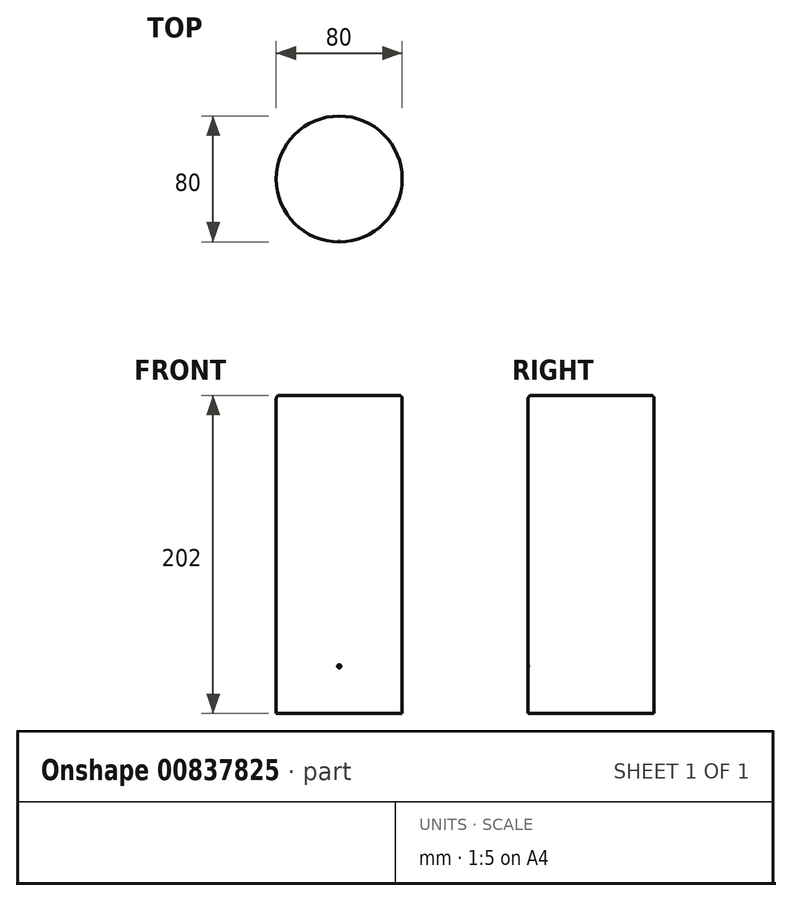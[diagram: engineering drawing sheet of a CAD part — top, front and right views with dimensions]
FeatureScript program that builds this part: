
annotation { "Feature Type Name" : "Feature", "Feature Type Description" : "" }
export const myFeature = defineFeature(function(context is Context, id is Id, definition is map)
    precondition{}
    {
        {
            var Q0;
            Q0=qCreatedBy(makeId("Front.planeOp"),FACE);
            var sketch = newSketch(context, id + "F0", { "sketchPlane" : qUnion([Q0])});
            skLineSegment(sketch, "E0", {"start": v(0, 0) * mm, "end": v(40, 0) * mm});
            skLineSegment(sketch, "E1", {"start": v(40, 0) * mm, "end": v(40, 50) * mm});
            skLineSegment(sketch, "E2", {"start": v(40, 50) * mm, "end": v(40, -150) * mm});
            skLineSegment(sketch, "E3", {"start": v(0, 0) * mm, "end": v(-40, 0) * mm});
            skLineSegment(sketch, "E4", {"start": v(-40, 0) * mm, "end": v(-40, 50) * mm});
            skLineSegment(sketch, "E5", {"start": v(-40, 50) * mm, "end": v(-40, -150) * mm});
            skLineSegment(sketch, "E6", {"start": v(-40, 50) * mm, "end": v(40, 50) * mm});
            skLineSegment(sketch, "E7", {"start": v(-40, -150) * mm, "end": v(40, -150) * mm});
            skLineSegment(sketch, "E8", {"start": v(0, 69.2) * mm, "end": v(0, -177.13) * mm});
            skPoint(sketch, "E8.startSnap0", {"position": v(0, 50) * mm});
            skPoint(sketch, "E8.endSnap0", {"position": v(0, -150) * mm});
            skSolve(sketch);
        }
        {
            var Q0;
            {var subQ0=sQuery(id+"F0.wireOp",EDGE,"E3");Q0=makeQuery(id+"F0.imprint","IMPRINT",FACE,{"disambiguationData":[TD([[makeQuery(id+"F0.imprint","IMPRINT",EDGE,{"derivedFrom":subQ0}),-1.0]])]});}
            var Q1;
            {var subQ0=sQuery(id+"F0.wireOp",EDGE,"E3");Q1=makeQuery(id+"F0.imprint","IMPRINT",FACE,{"disambiguationData":[TD([[makeQuery(id+"F0.imprint","IMPRINT",EDGE,{"derivedFrom":subQ0}),1.0]])]});}
            var Q2;
            Q2=sQuery(id+"F0.wireOp",EDGE,"E8");
            revolve(context, id + "F1", {"surfaceOperationType" : NewSurfaceOperationType.NEW, "entities" : qUnion([Q0, Q1]), "axis" : qUnion([Q2]), "revolveType" : RevolveType.FULL});
        }
        {
            var Q0;
            Q0=makeQuery(id+"F1.opRevolve","SWEPT_FACE",FACE,{"disambiguationData":[OSD([sQuery(id+"F0.wireOp",EDGE,"E7")])]});
            var sketch = newSketch(context, id + "F2", { "sketchPlane" : qUnion([Q0])});
            skCircle(sketch, "E9", {"center": v(0, 0) * mm, "radius": 40 * mm});
            skSolve(sketch);
        }
        {
            var Q0;
            Q0=makeQuery(id+"F1.opRevolve","SWEPT_FACE",FACE,{"disambiguationData":[OSD([sQuery(id+"F0.wireOp",EDGE,"E6")])]});
            fillet(context, id + "F3", {"entities" : qUnion([Q0]), "radius" : 2 * mm, "tangentPropagation" : true, "allowEdgeOverflow" : false});
        }
        {
            var Q0;
            Q0=makeQuery(id+"F2.imprint","IMPRINT",FACE,{"disambiguationData":[TD([[makeQuery(id+"F2.imprint","IMPRINT",EDGE,{"derivedFrom":sQuery(id+"F2.wireOp",EDGE,"E9")}),-1.0]])]});
            var Q1;
            Q1=sQuery(id+"F2.wireOp",EDGE,"E9");
            extrude(context, id + "F4", {"entities" : qUnion([Q0]), "operationType" : NewBodyOperationType.REMOVE, "surfaceEntities" : qUnion([Q1]), "oppositeDirection" : true, "depth" : 23 * mm, "offsetDistance" : 25 * mm});
        }
        {
            var Q0;
            Q0=qCreatedBy(makeId("Right.planeOp"),FACE);
            var sketch = newSketch(context, id + "F5", { "sketchPlane" : qUnion([Q0])});
            skLineSegment(sketch, "E10", {"start": v(40, 48) * mm, "end": v(40, -127) * mm});
            skLineSegment(sketch, "E11", {"start": v(-40, -127) * mm, "end": v(-40, 48) * mm});
            skLineSegment(sketch, "E12", {"start": v(-40, -127) * mm, "end": v(-40, -122) * mm});
            skCircle(sketch, "E13", {"center": v(-40, -122) * mm, "radius": 1 * mm});
            skSolve(sketch);
        }
        {
            var Q0;
            {var subQ0=sQuery(id+"F5.wireOp",EDGE,"E12");var subQ1=sQuery(id+"F5.wireOp",EDGE,"E11");var subQ2=makeQuery(id+"F5.imprint","INTERSECT",VERTEX,{"derivedFrom":[subQ1,subQ0]});Q0=makeQuery(id+"F5.imprint","IMPRINT",FACE,{"disambiguationData":[TD([[makeQuery(id+"F5.imprint","IMPRINT",EDGE,{"disambiguationData":[TD([[subQ2,-1.0]])],"derivedFrom":subQ1}),1.0]])]});}
            var Q1;
            Q1=sQuery(id+"F5.wireOp",EDGE,"E11");
            revolve(context, id + "F6", {"operationType" : NewBodyOperationType.REMOVE, "surfaceOperationType" : NewSurfaceOperationType.NEW, "entities" : qUnion([Q0]), "axis" : qUnion([Q1]), "revolveType" : RevolveType.FULL, "oppositeDirection" : true});
        }
        {
            var Q0;
            Q0=makeQuery(id+"F4.boolean.opBoolean","COPY",FACE,{"derivedFrom":makeQuery(id+"F4.opExtrude","CAP_FACE",FACE,{"disambiguationData":[OSD([sQuery(id+"F2.wireOp",EDGE,"E9")])],"isStart":false})});
            extrude(context, id + "F7", {"entities" : qUnion([Q0]), "operationType" : NewBodyOperationType.ADD, "depth" : 25 * mm, "offsetDistance" : 25 * mm});
        }
    });
